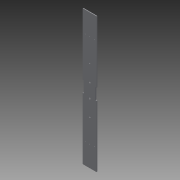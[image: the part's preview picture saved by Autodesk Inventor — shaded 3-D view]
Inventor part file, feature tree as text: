
AUTODESK INVENTOR PART (.ipt)
format: ipt  version: 2015 (Build 190159000, 159)  size: 113,152 bytes
history: native  units: mm
features: extrude x1, sketch x1
ambient origin geometry x8: Origin, YZ Plane, XZ Plane, XY Plane, X Axis, Y Axis, Z Axis, Center Point
bodies: Solid1 (feature_tree)
feature tree (2):
  extrude  "Extrusion1"  Depth=580.0mm
  sketch  "Sketch1"  dims[d0=60.0mm d1=580.0mm d16=200.0mm d17=3.0mm d18=10.0mm d19=2.0mm d20=2.0mm d21=2.0mm d27=8.0mm d28=6.0mm d29=60.0mm d30=3.0mm d31=0.0mm]
